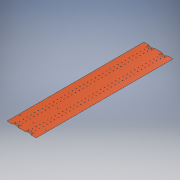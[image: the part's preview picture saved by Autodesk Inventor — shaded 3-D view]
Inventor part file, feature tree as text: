
AUTODESK INVENTOR PART (.ipt)
format: ipt  version: 2019 (Build 230136000, 136)  size: 440,320 bytes
history: native  units: mm
features: mirror x5, extrude x4, other x4
ambient origin geometry x8: Origin, YZ Plane, XZ Plane, XY Plane, X Axis, Y Axis, Z Axis, Center Point
bodies: Solid1 (feature_tree)
feature tree (13):
  extrude  "Skin Body"  Depth=2269.0mm
  extrude  "Feature Cut"  Depth=1134.5mm
  mirror  "Feature Cut Side Mirror"
  mirror  "Feature Cut Mirror"
  extrude  "End Cut"  Depth=424.0mm
  mirror  "End Cut Mirror"
  extrude  "Slot Cut"  Depth=212.0mm
  mirror  "Slot Cut Side Mirror"
  mirror  "Slot Cut Mirror"
  other  "Skin Scheme"
  other  "Feature Cut Outline"
  other  "End Cut Outline"
  other  "Slot Cut Outline"
